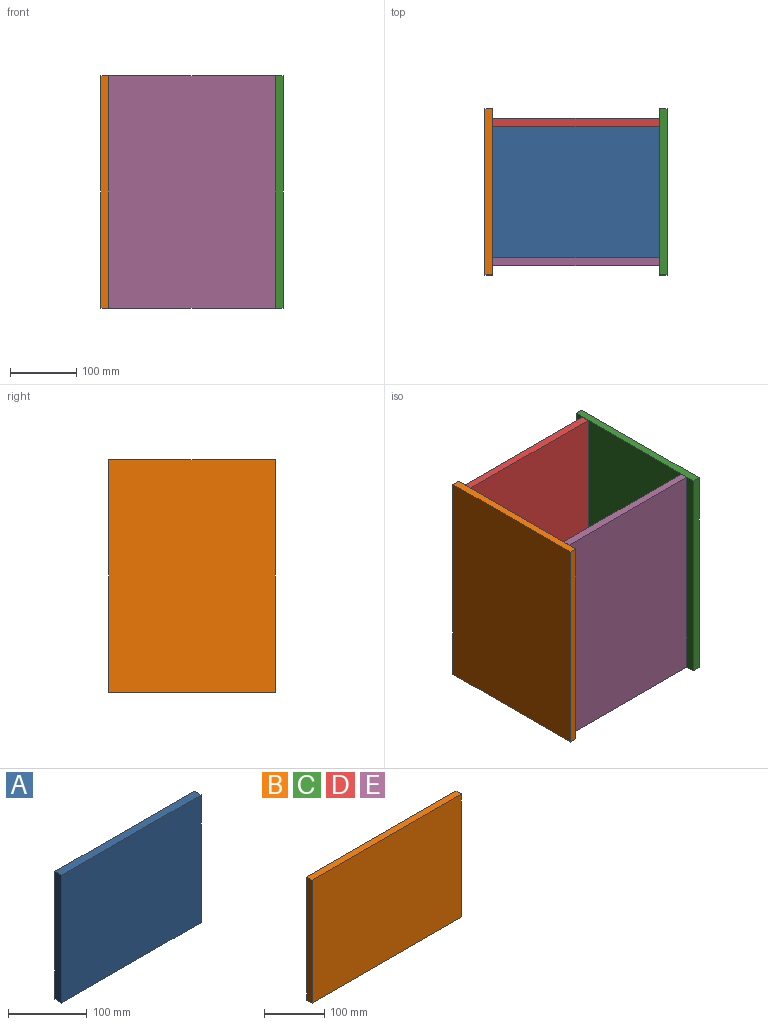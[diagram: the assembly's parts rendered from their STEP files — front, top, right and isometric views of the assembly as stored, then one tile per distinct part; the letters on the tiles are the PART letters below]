
ASSEMBLY  parts=5 mates=4
PART A: 6 faces, bbox 250x12x198 mm
  f0: plane 250x12mm, normal (0,0,1), area 3000mm2, adj f1,f3,f4,f5
  f1: plane 198x12mm, normal (-1,0,0), area 2376mm2, adj f0,f2,f4,f5
  f2: plane 250x12mm, normal (0,0,-1), area 3000mm2, adj f1,f3,f4,f5
  f3: plane 198x12mm, normal (1,0,0), area 2376mm2, adj f0,f2,f4,f5
  f4: plane 250x198mm, normal (0,-1,0), area 49500mm2, adj f0,f1,f2,f3
  f5: plane 250x198mm, normal (0,1,0), area 49500mm2, adj f0,f1,f2,f3
PART B: 6 faces, bbox 350x12x250 mm
  f0: plane 250x12mm, normal (-1,0,0), area 3000mm2, adj f1,f3,f4,f5
  f1: plane 350x12mm, normal (0,0,-1), area 4200mm2, adj f0,f2,f4,f5
  f2: plane 250x12mm, normal (1,0,0), area 3000mm2, adj f1,f3,f4,f5
  f3: plane 350x12mm, normal (0,0,1), area 4200mm2, adj f0,f2,f4,f5
  f4: plane 350x250mm, normal (0,-1,0), area 87500mm2, adj f0,f1,f2,f3
  f5: plane 350x250mm, normal (0,1,0), area 87500mm2, adj f0,f1,f2,f3
PART C: same geometry as B
PART D: same geometry as B
PART E: same geometry as B
PLACE A rot(axis=(-1,0,0),90deg) t=(71.94,-83.65,-155.28)mm fixed
PLACE B rot(axis=(-0.58,-0.58,-0.58),120deg) t=(-53.06,-83.65,19.72)mm
PLACE C rot(axis=(-0.58,-0.58,-0.58),120deg) t=(208.94,-83.65,19.72)mm
PLACE D rot(axis=(0,1,0),90deg) t=(71.94,27.35,19.72)mm
PLACE E rot(axis=(0.71,0,-0.71),180deg) t=(71.94,-194.65,19.72)mm
MATE fastened A.f3 <-> C.f4  axis (1,0,0) through (196.94,-83.65,-149.28)mm
MATE fastened A.f2 <-> E.f4  axis (0,-1,0) through (71.94,-182.65,-149.28)mm
MATE fastened A.f1 <-> B.f5  axis (-1,0,0) through (-53.06,-83.65,-149.28)mm
MATE fastened A.f0 <-> D.f4  axis (0,1,0) through (71.94,15.35,-149.28)mm
